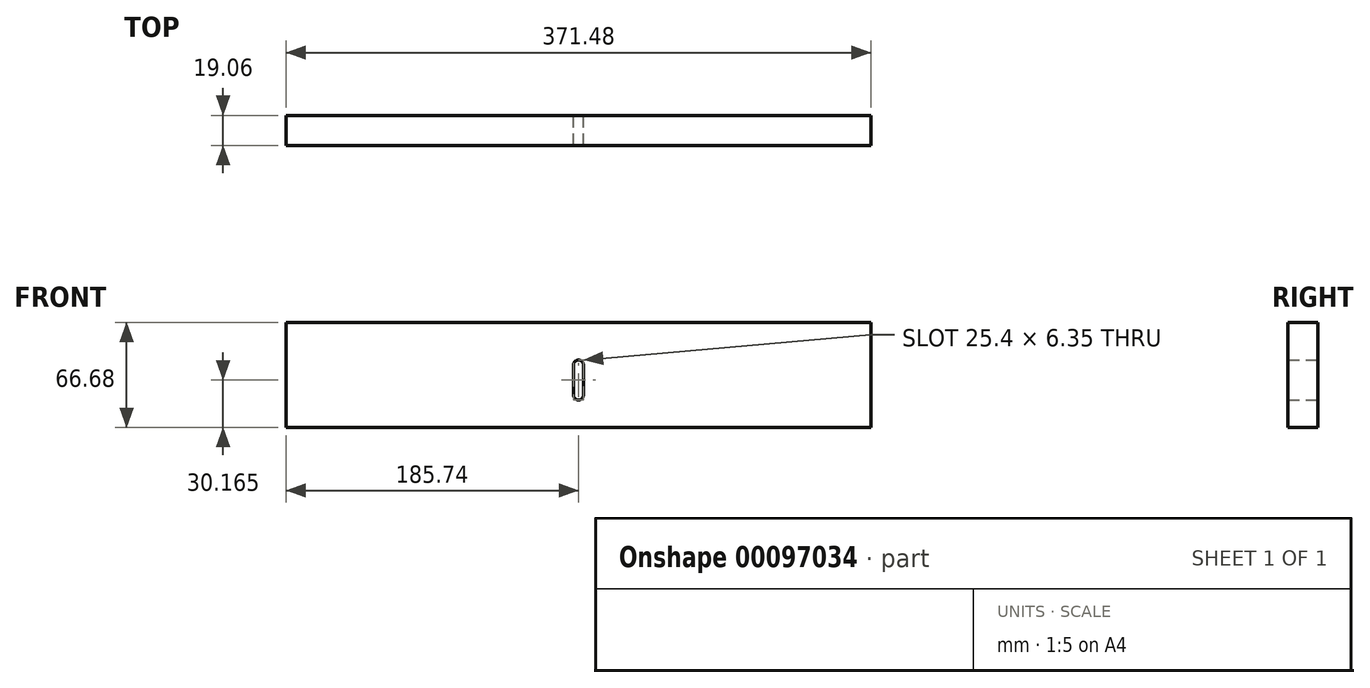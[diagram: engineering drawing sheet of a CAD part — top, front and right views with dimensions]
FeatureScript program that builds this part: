
annotation { "Feature Type Name" : "Feature", "Feature Type Description" : "" }
export const myFeature = defineFeature(function(context is Context, id is Id, definition is map)
    precondition{}
    {
        {
            var Q0;
            Q0=qCreatedBy(makeId("Front.planeOp"),FACE);
            var sketch = newSketch(context, id + "F0", { "sketchPlane" : qUnion([Q0])});
            skLineSegment(sketch, "E0.bottom", {"start": v(-185.74, 33.34) * mm, "end": v(185.74, 33.34) * mm});
            skLineSegment(sketch, "E0.top", {"start": v(-185.74, -33.34) * mm, "end": v(185.74, -33.34) * mm});
            skLineSegment(sketch, "E0.left", {"start": v(-185.74, 33.34) * mm, "end": v(-185.74, -33.34) * mm});
            skLineSegment(sketch, "E0.right", {"start": v(185.74, 33.34) * mm, "end": v(185.74, -33.34) * mm});
            skPoint(sketch, "E0.middle", {"position": v(0, 0) * mm});
            skArc(sketch, "E1", {"start": v(3.18, 6.35) * mm, "mid": v(0, 9.52) * mm, "end": v(-3.18, 6.35) * mm});
            skArc(sketch, "E2", {"start": v(-3.17, -12.7) * mm, "mid": v(0, -15.88) * mm, "end": v(3.18, -12.7) * mm});
            skLineSegment(sketch, "E3", {"start": v(-3.18, 6.35) * mm, "end": v(-3.18, -12.7) * mm});
            skLineSegment(sketch, "E4", {"start": v(3.18, -12.7) * mm, "end": v(3.18, 6.35) * mm});
            skText(sketch, "E5", { "text": "3/4 pine\n", "fontName": "OpenSans-Regular.ttf"});
            const initialGuessF0  = {"E5": [-0.05748, -0.06908, 1, 0, 0.02087]};
            skSetInitialGuess(sketch, initialGuessF0);
            skSolve(sketch);
        }
        {
            var Q0;
            Q0 = qSketchRegion(id + "F0", true);
            extrude(context, id + "F1", {"entities" : qUnion([Q0]), "endBound" : BoundingType.SYMMETRIC, "depth" : 19.05 * mm});
        }
        {
            var Q0;
            Q0=makeQuery(id+"F1.opExtrude","SWEPT_BODY",BODY,{"disambiguationData":[OSD([sQuery(id+"F0.wireOp",EDGE,"E5.sketch_text.stroke-0"),sQuery(id+"F0.wireOp",EDGE,"E5.sketch_text.stroke-1"),sQuery(id+"F0.wireOp",EDGE,"E5.sketch_text.stroke-2"),sQuery(id+"F0.wireOp",EDGE,"E5.sketch_text.stroke-3"),sQuery(id+"F0.wireOp",EDGE,"E5.sketch_text.stroke-4"),sQuery(id+"F0.wireOp",EDGE,"E5.sketch_text.stroke-5"),sQuery(id+"F0.wireOp",EDGE,"E5.sketch_text.stroke-6"),sQuery(id+"F0.wireOp",EDGE,"E5.sketch_text.stroke-7"),sQuery(id+"F0.wireOp",EDGE,"E5.sketch_text.stroke-8"),sQuery(id+"F0.wireOp",EDGE,"E5.sketch_text.stroke-9"),sQuery(id+"F0.wireOp",EDGE,"E5.sketch_text.stroke-10"),sQuery(id+"F0.wireOp",EDGE,"E5.sketch_text.stroke-11"),sQuery(id+"F0.wireOp",EDGE,"E5.sketch_text.stroke-12"),sQuery(id+"F0.wireOp",EDGE,"E5.sketch_text.stroke-13"),sQuery(id+"F0.wireOp",EDGE,"E5.sketch_text.stroke-14"),sQuery(id+"F0.wireOp",EDGE,"E5.sketch_text.stroke-15"),sQuery(id+"F0.wireOp",EDGE,"E5.sketch_text.stroke-16"),sQuery(id+"F0.wireOp",EDGE,"E5.sketch_text.stroke-17"),sQuery(id+"F0.wireOp",EDGE,"E5.sketch_text.stroke-18"),sQuery(id+"F0.wireOp",EDGE,"E5.sketch_text.stroke-19"),sQuery(id+"F0.wireOp",EDGE,"E5.sketch_text.stroke-20"),sQuery(id+"F0.wireOp",EDGE,"E5.sketch_text.stroke-21"),sQuery(id+"F0.wireOp",EDGE,"E5.sketch_text.stroke-22"),sQuery(id+"F0.wireOp",EDGE,"E5.sketch_text.stroke-23"),sQuery(id+"F0.wireOp",EDGE,"E5.sketch_text.stroke-24"),sQuery(id+"F0.wireOp",EDGE,"E5.sketch_text.stroke-25"),sQuery(id+"F0.wireOp",EDGE,"E5.sketch_text.stroke-26"),sQuery(id+"F0.wireOp",EDGE,"E5.sketch_text.stroke-27")])]});
            deleteBodies(context, id + "F2", {"entities" : qUnion([Q0])});
        }
        {
            var Q0;
            Q0=makeQuery(id+"F1.opExtrude","SWEPT_BODY",BODY,{"disambiguationData":[OSD([sQuery(id+"F0.wireOp",EDGE,"E5.sketch_text.stroke-28"),sQuery(id+"F0.wireOp",EDGE,"E5.sketch_text.stroke-29"),sQuery(id+"F0.wireOp",EDGE,"E5.sketch_text.stroke-30"),sQuery(id+"F0.wireOp",EDGE,"E5.sketch_text.stroke-31")])]});
            var Q1;
            Q1=makeQuery(id+"F1.opExtrude","SWEPT_BODY",BODY,{"disambiguationData":[OSD([sQuery(id+"F0.wireOp",EDGE,"E5.sketch_text.stroke-32"),sQuery(id+"F0.wireOp",EDGE,"E5.sketch_text.stroke-33"),sQuery(id+"F0.wireOp",EDGE,"E5.sketch_text.stroke-34"),sQuery(id+"F0.wireOp",EDGE,"E5.sketch_text.stroke-35"),sQuery(id+"F0.wireOp",EDGE,"E5.sketch_text.stroke-36"),sQuery(id+"F0.wireOp",EDGE,"E5.sketch_text.stroke-37"),sQuery(id+"F0.wireOp",EDGE,"E5.sketch_text.stroke-38"),sQuery(id+"F0.wireOp",EDGE,"E5.sketch_text.stroke-39"),sQuery(id+"F0.wireOp",EDGE,"E5.sketch_text.stroke-40"),sQuery(id+"F0.wireOp",EDGE,"E5.sketch_text.stroke-41"),sQuery(id+"F0.wireOp",EDGE,"E5.sketch_text.stroke-42"),sQuery(id+"F0.wireOp",EDGE,"E5.sketch_text.stroke-43"),sQuery(id+"F0.wireOp",EDGE,"E5.sketch_text.stroke-44"),sQuery(id+"F0.wireOp",EDGE,"E5.sketch_text.stroke-45"),sQuery(id+"F0.wireOp",EDGE,"E5.sketch_text.stroke-46"),sQuery(id+"F0.wireOp",EDGE,"E5.sketch_text.stroke-47"),sQuery(id+"F0.wireOp",EDGE,"E5.sketch_text.stroke-48")])]});
            var Q2;
            Q2=makeQuery(id+"F1.opExtrude","SWEPT_BODY",BODY,{"disambiguationData":[OSD([sQuery(id+"F0.wireOp",EDGE,"E5.sketch_text.stroke-49"),sQuery(id+"F0.wireOp",EDGE,"E5.sketch_text.stroke-50"),sQuery(id+"F0.wireOp",EDGE,"E5.sketch_text.stroke-51"),sQuery(id+"F0.wireOp",EDGE,"E5.sketch_text.stroke-52"),sQuery(id+"F0.wireOp",EDGE,"E5.sketch_text.stroke-53"),sQuery(id+"F0.wireOp",EDGE,"E5.sketch_text.stroke-54"),sQuery(id+"F0.wireOp",EDGE,"E5.sketch_text.stroke-55"),sQuery(id+"F0.wireOp",EDGE,"E5.sketch_text.stroke-56"),sQuery(id+"F0.wireOp",EDGE,"E5.sketch_text.stroke-57"),sQuery(id+"F0.wireOp",EDGE,"E5.sketch_text.stroke-58"),sQuery(id+"F0.wireOp",EDGE,"E5.sketch_text.stroke-59"),sQuery(id+"F0.wireOp",EDGE,"E5.sketch_text.stroke-60"),sQuery(id+"F0.wireOp",EDGE,"E5.sketch_text.stroke-61"),sQuery(id+"F0.wireOp",EDGE,"E5.sketch_text.stroke-62"),sQuery(id+"F0.wireOp",EDGE,"E5.sketch_text.stroke-63"),sQuery(id+"F0.wireOp",EDGE,"E5.sketch_text.stroke-64"),sQuery(id+"F0.wireOp",EDGE,"E5.sketch_text.stroke-65"),sQuery(id+"F0.wireOp",EDGE,"E5.sketch_text.stroke-66"),sQuery(id+"F0.wireOp",EDGE,"E5.sketch_text.stroke-67"),sQuery(id+"F0.wireOp",EDGE,"E5.sketch_text.stroke-68"),sQuery(id+"F0.wireOp",EDGE,"E5.sketch_text.stroke-69"),sQuery(id+"F0.wireOp",EDGE,"E5.sketch_text.stroke-70"),sQuery(id+"F0.wireOp",EDGE,"E5.sketch_text.stroke-71"),sQuery(id+"F0.wireOp",EDGE,"E5.sketch_text.stroke-72"),sQuery(id+"F0.wireOp",EDGE,"E5.sketch_text.stroke-73")])]});
            var Q3;
            Q3=makeQuery(id+"F1.opExtrude","SWEPT_BODY",BODY,{"disambiguationData":[OSD([sQuery(id+"F0.wireOp",EDGE,"E5.sketch_text.stroke-74"),sQuery(id+"F0.wireOp",EDGE,"E5.sketch_text.stroke-75"),sQuery(id+"F0.wireOp",EDGE,"E5.sketch_text.stroke-76"),sQuery(id+"F0.wireOp",EDGE,"E5.sketch_text.stroke-77")])]});
            var Q4;
            Q4=makeQuery(id+"F1.opExtrude","SWEPT_BODY",BODY,{"disambiguationData":[OSD([sQuery(id+"F0.wireOp",EDGE,"E5.sketch_text.stroke-78"),sQuery(id+"F0.wireOp",EDGE,"E5.sketch_text.stroke-79"),sQuery(id+"F0.wireOp",EDGE,"E5.sketch_text.stroke-80"),sQuery(id+"F0.wireOp",EDGE,"E5.sketch_text.stroke-81"),sQuery(id+"F0.wireOp",EDGE,"E5.sketch_text.stroke-82"),sQuery(id+"F0.wireOp",EDGE,"E5.sketch_text.stroke-83"),sQuery(id+"F0.wireOp",EDGE,"E5.sketch_text.stroke-84"),sQuery(id+"F0.wireOp",EDGE,"E5.sketch_text.stroke-85")])]});
            deleteBodies(context, id + "F3", {"entities" : qUnion([Q0, Q1, Q2, Q3, Q4])});
        }
        {
            var Q0;
            Q0=makeQuery(id+"F1.opExtrude","SWEPT_BODY",BODY,{"disambiguationData":[OSD([sQuery(id+"F0.wireOp",EDGE,"E5.sketch_text.stroke-86"),sQuery(id+"F0.wireOp",EDGE,"E5.sketch_text.stroke-87"),sQuery(id+"F0.wireOp",EDGE,"E5.sketch_text.stroke-88"),sQuery(id+"F0.wireOp",EDGE,"E5.sketch_text.stroke-89"),sQuery(id+"F0.wireOp",EDGE,"E5.sketch_text.stroke-90"),sQuery(id+"F0.wireOp",EDGE,"E5.sketch_text.stroke-91"),sQuery(id+"F0.wireOp",EDGE,"E5.sketch_text.stroke-92"),sQuery(id+"F0.wireOp",EDGE,"E5.sketch_text.stroke-93"),sQuery(id+"F0.wireOp",EDGE,"E5.sketch_text.stroke-94"),sQuery(id+"F0.wireOp",EDGE,"E5.sketch_text.stroke-95"),sQuery(id+"F0.wireOp",EDGE,"E5.sketch_text.stroke-96"),sQuery(id+"F0.wireOp",EDGE,"E5.sketch_text.stroke-97"),sQuery(id+"F0.wireOp",EDGE,"E5.sketch_text.stroke-98"),sQuery(id+"F0.wireOp",EDGE,"E5.sketch_text.stroke-99"),sQuery(id+"F0.wireOp",EDGE,"E5.sketch_text.stroke-100"),sQuery(id+"F0.wireOp",EDGE,"E5.sketch_text.stroke-101"),sQuery(id+"F0.wireOp",EDGE,"E5.sketch_text.stroke-102")])]});
            deleteBodies(context, id + "F4", {"entities" : qUnion([Q0])});
        }
        {
            var Q0;
            Q0=makeQuery(id+"F1.opExtrude","SWEPT_BODY",BODY,{"disambiguationData":[OSD([sQuery(id+"F0.wireOp",EDGE,"E5.sketch_text.stroke-103"),sQuery(id+"F0.wireOp",EDGE,"E5.sketch_text.stroke-104"),sQuery(id+"F0.wireOp",EDGE,"E5.sketch_text.stroke-105"),sQuery(id+"F0.wireOp",EDGE,"E5.sketch_text.stroke-106"),sQuery(id+"F0.wireOp",EDGE,"E5.sketch_text.stroke-107"),sQuery(id+"F0.wireOp",EDGE,"E5.sketch_text.stroke-108"),sQuery(id+"F0.wireOp",EDGE,"E5.sketch_text.stroke-109"),sQuery(id+"F0.wireOp",EDGE,"E5.sketch_text.stroke-110"),sQuery(id+"F0.wireOp",EDGE,"E5.sketch_text.stroke-111"),sQuery(id+"F0.wireOp",EDGE,"E5.sketch_text.stroke-112"),sQuery(id+"F0.wireOp",EDGE,"E5.sketch_text.stroke-113"),sQuery(id+"F0.wireOp",EDGE,"E5.sketch_text.stroke-114"),sQuery(id+"F0.wireOp",EDGE,"E5.sketch_text.stroke-115"),sQuery(id+"F0.wireOp",EDGE,"E5.sketch_text.stroke-116"),sQuery(id+"F0.wireOp",EDGE,"E5.sketch_text.stroke-117"),sQuery(id+"F0.wireOp",EDGE,"E5.sketch_text.stroke-118"),sQuery(id+"F0.wireOp",EDGE,"E5.sketch_text.stroke-119"),sQuery(id+"F0.wireOp",EDGE,"E5.sketch_text.stroke-120"),sQuery(id+"F0.wireOp",EDGE,"E5.sketch_text.stroke-121")])]});
            deleteBodies(context, id + "F5", {"entities" : qUnion([Q0])});
        }
    });
